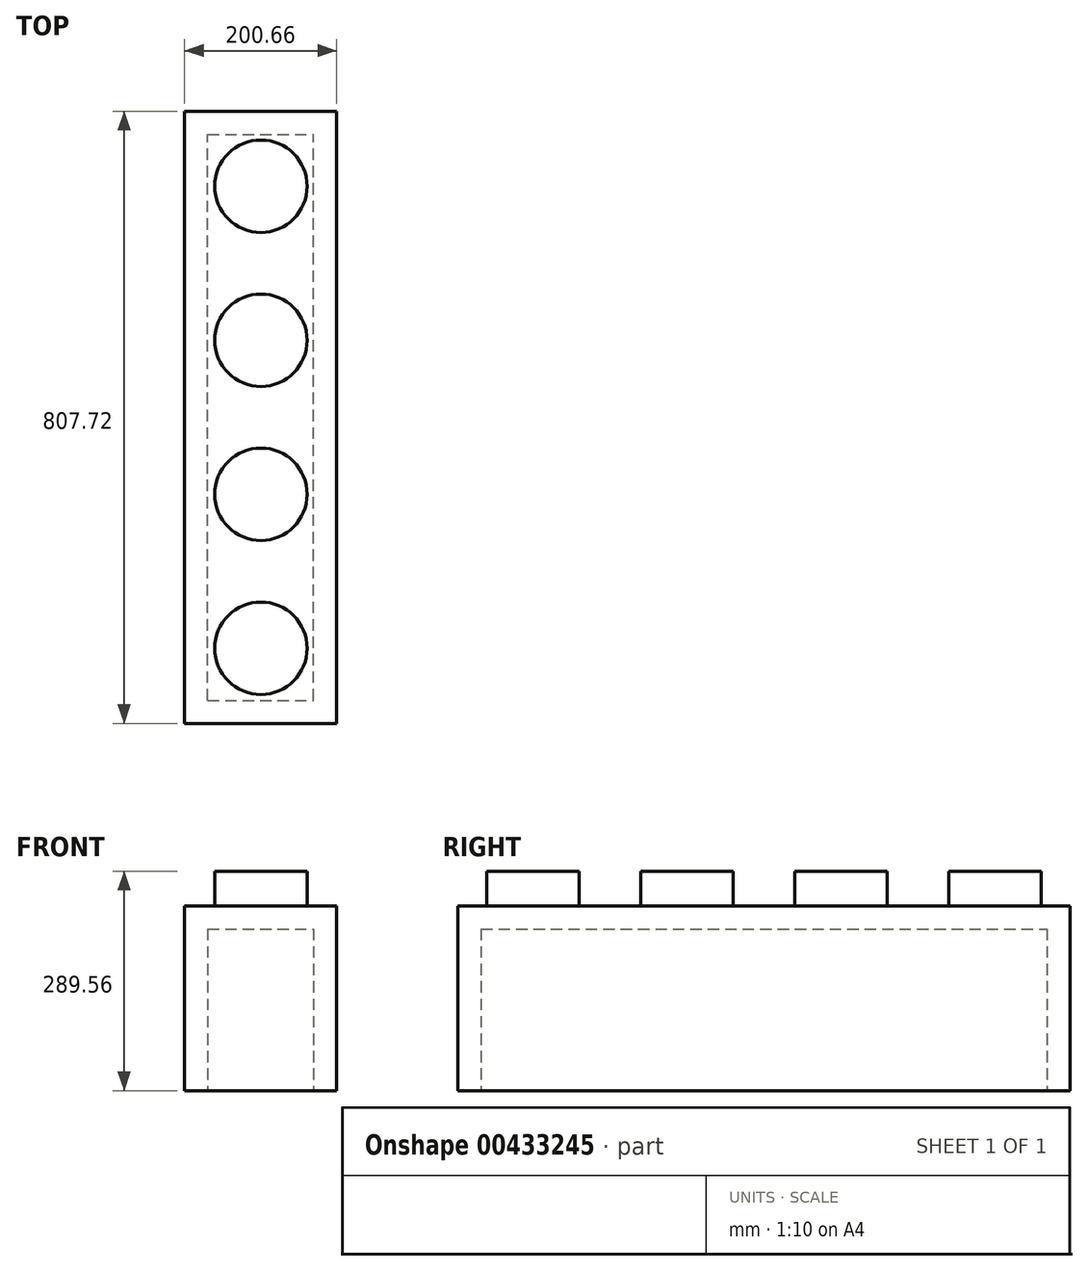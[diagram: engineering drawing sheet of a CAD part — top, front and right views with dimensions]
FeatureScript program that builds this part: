
annotation { "Feature Type Name" : "Feature", "Feature Type Description" : "" }
export const myFeature = defineFeature(function(context is Context, id is Id, definition is map)
    precondition{}
    {
        {
            var Q0;
            Q0=qCreatedBy(makeId("Top.planeOp"),FACE);
            var sketch = newSketch(context, id + "F0", { "sketchPlane" : qUnion([Q0])});
            skLineSegment(sketch, "E0.bottom", {"start": v(-100.6, 656.22) * mm, "end": v(100.07, 656.22) * mm});
            skLineSegment(sketch, "E0.top", {"start": v(-100.6, -151.5) * mm, "end": v(100.07, -151.5) * mm});
            skLineSegment(sketch, "E0.left", {"start": v(-100.6, 656.22) * mm, "end": v(-100.6, -151.5) * mm});
            skLineSegment(sketch, "E0.right", {"start": v(100.07, 656.22) * mm, "end": v(100.07, -151.5) * mm});
            skSolve(sketch);
        }
        {
            var Q0;
            Q0=makeQuery(id+"F0.imprint","IMPRINT",FACE,{"disambiguationData":[TD([[makeQuery(id+"F0.imprint","IMPRINT",EDGE,{"derivedFrom":sQuery(id+"F0.wireOp",EDGE,"E0.bottom")}),-1.0]])]});
            extrude(context, id + "F1", {"entities" : qUnion([Q0]), "depth" : 243.84 * mm});
        }
        {
            var Q0;
            Q0=makeQuery(id+"F1.opExtrude","CAP_FACE",FACE,{"disambiguationData":[OSD([sQuery(id+"F0.wireOp",EDGE,"E0.bottom"),sQuery(id+"F0.wireOp",EDGE,"E0.top"),sQuery(id+"F0.wireOp",EDGE,"E0.left"),sQuery(id+"F0.wireOp",EDGE,"E0.right")])],"isStart":false});
            var sketch = newSketch(context, id + "F2", { "sketchPlane" : qUnion([Q0])});
            skCircle(sketch, "E1", {"center": v(0, -52.44) * mm, "radius": 60.96 * mm});
            skCircle(sketch, "E2.0.1.0", {"center": v(0, 150.76) * mm, "radius": 60.96 * mm});
            skCircle(sketch, "E2.0.2.0", {"center": v(0, 353.96) * mm, "radius": 60.96 * mm});
            skCircle(sketch, "E2.0.3.0", {"center": v(0, 557.16) * mm, "radius": 60.96 * mm});
            skLineSegment(sketch, "E2.direction1", {"start": v(0, -52.44) * mm, "end": v(25.4, -52.44) * mm, "construction": true});
            skLineSegment(sketch, "E2.direction2", {"start": v(0, -52.44) * mm, "end": v(0, 150.76) * mm, "construction": true});
            skSolve(sketch);
        }
        {
            var Q0;
            Q0=makeQuery(id+"F2.imprint","IMPRINT",FACE,{"disambiguationData":[TD([[makeQuery(id+"F2.imprint","IMPRINT",EDGE,{"derivedFrom":sQuery(id+"F2.wireOp",EDGE,"E1")}),1.0]])]});
            var Q1;
            Q1=makeQuery(id+"F2.imprint","IMPRINT",FACE,{"disambiguationData":[TD([[makeQuery(id+"F2.imprint","IMPRINT",EDGE,{"derivedFrom":sQuery(id+"F2.wireOp",EDGE,"E2.0.1.0")}),1.0]])]});
            var Q2;
            Q2=makeQuery(id+"F2.imprint","IMPRINT",FACE,{"disambiguationData":[TD([[makeQuery(id+"F2.imprint","IMPRINT",EDGE,{"derivedFrom":sQuery(id+"F2.wireOp",EDGE,"E2.0.2.0")}),1.0]])]});
            var Q3;
            Q3=makeQuery(id+"F2.imprint","IMPRINT",FACE,{"disambiguationData":[TD([[makeQuery(id+"F2.imprint","IMPRINT",EDGE,{"derivedFrom":sQuery(id+"F2.wireOp",EDGE,"E2.0.3.0")}),1.0]])]});
            extrude(context, id + "F3", {"entities" : qUnion([Q0, Q1, Q2, Q3]), "operationType" : NewBodyOperationType.ADD, "depth" : 45.72 * mm});
        }
        {
            var Q0;
            Q0=makeQuery(id+"F1.opExtrude","CAP_FACE",FACE,{"disambiguationData":[OSD([sQuery(id+"F0.wireOp",EDGE,"E0.bottom"),sQuery(id+"F0.wireOp",EDGE,"E0.top"),sQuery(id+"F0.wireOp",EDGE,"E0.left"),sQuery(id+"F0.wireOp",EDGE,"E0.right")])],"isStart":true});
            var sketch = newSketch(context, id + "F4", { "sketchPlane" : qUnion([Q0])});
            skLineSegment(sketch, "E3.bottom", {"start": v(-70.11, 121.02) * mm, "end": v(69.59, 121.02) * mm});
            skLineSegment(sketch, "E3.top", {"start": v(-70.11, -625.74) * mm, "end": v(69.59, -625.74) * mm});
            skLineSegment(sketch, "E3.left", {"start": v(-70.11, 121.02) * mm, "end": v(-70.11, -625.74) * mm});
            skLineSegment(sketch, "E3.right", {"start": v(69.59, 121.02) * mm, "end": v(69.59, -625.74) * mm});
            skSolve(sketch);
        }
        {
            var Q0;
            Q0=makeQuery(id+"F4.imprint","IMPRINT",FACE,{"disambiguationData":[TD([[makeQuery(id+"F4.imprint","IMPRINT",EDGE,{"derivedFrom":sQuery(id+"F4.wireOp",EDGE,"E3.bottom")}),-1.0]])]});
            extrude(context, id + "F5", {"entities" : qUnion([Q0]), "operationType" : NewBodyOperationType.REMOVE, "oppositeDirection" : true, "depth" : 213.36 * mm});
        }
    });
